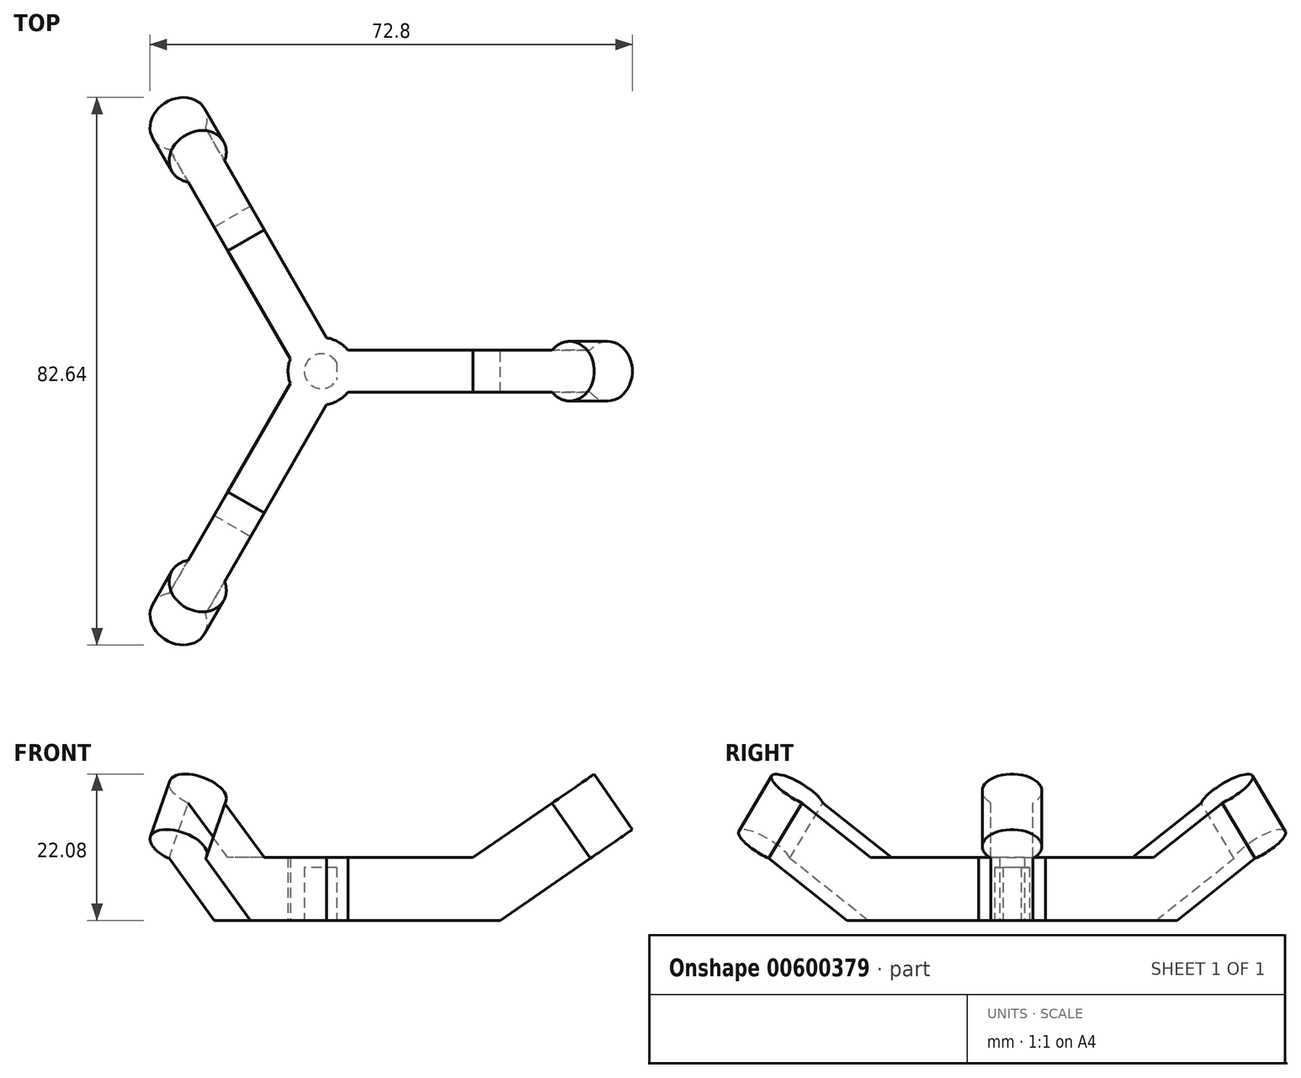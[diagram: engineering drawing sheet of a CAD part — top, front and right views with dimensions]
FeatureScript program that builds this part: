
annotation { "Feature Type Name" : "Feature", "Feature Type Description" : "" }
export const myFeature = defineFeature(function(context is Context, id is Id, definition is map)
    precondition{}
    {
        {
            var Q0;
            Q0=qCreatedBy(makeId("Front.planeOp"),FACE);
            var sketch = newSketch(context, id + "F0", { "sketchPlane" : qUnion([Q0])});
            skCircle(sketch, "E0", {"center": v(0, 59.06) * mm, "radius": 63.5 * mm, "construction": true});
            skCircle(sketch, "E1", {"center": v(38.1, 3.57) * mm, "radius": 5 * mm, "construction": true});
            skLineSegment(sketch, "E2", {"start": v(33.16, 2.82) * mm, "end": v(40.58, 7.9) * mm, "construction": true});
            skLineSegment(sketch, "E3", {"start": v(33.16, 2.82) * mm, "end": v(33.72, 2) * mm, "construction": true});
            skLineSegment(sketch, "E4", {"start": v(33.72, 2) * mm, "end": v(41.14, 7.09) * mm, "construction": true});
            skLineSegment(sketch, "E5", {"start": v(41.14, 7.09) * mm, "end": v(40.58, 7.9) * mm, "construction": true});
            skLineSegment(sketch, "E6", {"start": v(38.1, 3.57) * mm, "end": v(0, 59.06) * mm, "construction": true});
            skLineSegment(sketch, "E7", {"start": v(0, -6.99) * mm, "end": v(2.63, -6.99) * mm});
            skLineSegment(sketch, "E8", {"start": v(2.63, -6.99) * mm, "end": v(2.63, -14.99) * mm});
            skLineSegment(sketch, "E9", {"start": v(0, -6.99) * mm, "end": v(0, -5.49) * mm});
            skLineSegment(sketch, "E10", {"start": v(0, -5.49) * mm, "end": v(22.83, -5.49) * mm});
            skLineSegment(sketch, "E11", {"start": v(22.83, -5.49) * mm, "end": v(33.72, 2) * mm});
            skLineSegment(sketch, "E12", {"start": v(33.72, 2) * mm, "end": v(41.14, 7.09) * mm});
            skLineSegment(sketch, "E13", {"start": v(2.63, -14.99) * mm, "end": v(26.95, -14.98) * mm});
            skLineSegment(sketch, "E14", {"start": v(26.95, -14.98) * mm, "end": v(46.9, -1.3) * mm});
            skLineSegment(sketch, "E15", {"start": v(46.9, -1.3) * mm, "end": v(41.14, 7.09) * mm});
            skLineSegment(sketch, "E16", {"start": v(0, 0) * mm, "end": v(0, -5.49) * mm, "construction": true});
            skSolve(sketch);
        }
        {
            var Q0;
            Q0 = qSketchRegion(id + "F0", true);
            extrude(context, id + "F1", {"entities" : qUnion([Q0]), "endBound" : BoundingType.SYMMETRIC, "depth" : 6.35 * mm, "offsetDistance" : 25.4 * mm});
        }
        {
            var Q0;
            Q0=makeQuery(id+"F1.opExtrude","SWEPT_FACE",FACE,{"disambiguationData":[OSD([sQuery(id+"F0.wireOp",EDGE,"E11"),sQuery(id+"F0.wireOp",EDGE,"E12")])]});
            var sketch = newSketch(context, id + "F2", { "sketchPlane" : qUnion([Q0])});
            skLineSegment(sketch, "E17.0", {"start": v(37.93, -3.18) * mm, "end": v(37.93, 3.17) * mm});
            skLineSegment(sketch, "E18.0", {"start": v(15.72, 3.18) * mm, "end": v(37.93, 3.18) * mm});
            skLineSegment(sketch, "E19.0", {"start": v(15.72, -3.18) * mm, "end": v(37.93, -3.18) * mm});
            skCircle(sketch, "E20", {"center": v(33.43, 0) * mm, "radius": 4.5 * mm});
            skSolve(sketch);
        }
        {
            var Q0;
            {var subQ0=sQuery(id+"F2.wireOp",EDGE,"E20");var subQ1=sQuery(id+"F2.wireOp",EDGE,"E18.0");var subQ2=makeQuery(id+"F2.imprint","INTERSECT",VERTEX,{"disambiguationData":[OD(0.0)],"derivedFrom":[subQ1,subQ0]});Q0=makeQuery(id+"F2.imprint","IMPRINT",FACE,{"disambiguationData":[TD([[makeQuery(id+"F2.imprint","IMPRINT",EDGE,{"disambiguationData":[TD([[subQ2,-1.0]])],"derivedFrom":subQ1}),1.0]])]});}
            var Q1;
            {var subQ0=sQuery(id+"F2.wireOp",EDGE,"E20");var subQ1=sQuery(id+"F2.wireOp",EDGE,"E19.0");var subQ2=makeQuery(id+"F2.imprint","INTERSECT",VERTEX,{"disambiguationData":[OD(0.0)],"derivedFrom":[subQ1,subQ0]});Q1=makeQuery(id+"F2.imprint","IMPRINT",FACE,{"disambiguationData":[TD([[makeQuery(id+"F2.imprint","IMPRINT",EDGE,{"disambiguationData":[TD([[subQ2,-1.0]])],"derivedFrom":subQ1}),-1.0]])]});}
            var Q2;
            {var subQ0=sQuery(id+"F2.wireOp",EDGE,"E20");var subQ1=sQuery(id+"F2.wireOp",EDGE,"E18.0");var subQ2=makeQuery(id+"F2.imprint","INTERSECT",VERTEX,{"disambiguationData":[OD(0.0)],"derivedFrom":[subQ1,subQ0]});Q2=makeQuery(id+"F2.imprint","IMPRINT",FACE,{"disambiguationData":[TD([[makeQuery(id+"F2.imprint","IMPRINT",EDGE,{"disambiguationData":[TD([[subQ2,-1.0]])],"derivedFrom":subQ1}),-1.0]])]});}
            var Q3;
            Q3=makeQuery(id+"F1.opExtrude","SWEPT_FACE",FACE,{"disambiguationData":[OSD([sQuery(id+"F0.wireOp",EDGE,"E14")])]});
            extrude(context, id + "F3", {"entities" : qUnion([Q0, Q1, Q2]), "operationType" : NewBodyOperationType.ADD, "endBound" : BoundingType.UP_TO_SURFACE, "oppositeDirection" : true, "depth" : 25.4 * mm, "endBoundEntityFace" : qUnion([Q3]), "offsetDistance" : 25.4 * mm});
        }
        {
            var Q0;
            Q0=makeQuery(id+"F3.boolean.opBoolean","MERGE",FACE,{"derivedFrom":[makeQuery(id+"F1.opExtrude","SWEPT_FACE",FACE,{"disambiguationData":[OSD([sQuery(id+"F0.wireOp",EDGE,"E11"),sQuery(id+"F0.wireOp",EDGE,"E12")])]}),makeQuery(id+"F3.opExtrude","CAP_FACE",FACE,{"disambiguationData":[OSD([sQuery(id+"F2.wireOp",EDGE,"E20")])],"isStart":true})]});
            var sketch = newSketch(context, id + "F4", { "sketchPlane" : qUnion([Q0])});
            skLineSegment(sketch, "E21.0.0", {"start": v(37.93, -3.18) * mm, "end": v(37.93, 3.17) * mm});
            skLineSegment(sketch, "E21.0.1", {"start": v(37.93, 3.18) * mm, "end": v(36.62, 3.18) * mm});
            skArc(sketch, "E21.0.2", {"start": v(36.62, 3.17) * mm, "mid": v(33.43, 4.5) * mm, "end": v(30.24, 3.18) * mm});
            skLineSegment(sketch, "E21.0.3", {"start": v(30.24, 3.18) * mm, "end": v(15.72, 3.18) * mm});
            skLineSegment(sketch, "E21.0.4", {"start": v(15.72, 3.17) * mm, "end": v(15.72, -3.18) * mm});
            skLineSegment(sketch, "E21.0.5", {"start": v(15.72, -3.18) * mm, "end": v(30.24, -3.18) * mm});
            skArc(sketch, "E21.0.6", {"start": v(30.24, -3.18) * mm, "mid": v(33.43, -4.5) * mm, "end": v(36.62, -3.17) * mm});
            skLineSegment(sketch, "E21.0.7", {"start": v(36.62, -3.18) * mm, "end": v(37.93, -3.18) * mm});
            skCircle(sketch, "E22", {"center": v(33.43, 0) * mm, "radius": 4.5 * mm});
            skSolve(sketch);
        }
        {
            var Q0;
            {var subQ0=sQuery(id+"F4.wireOp",EDGE,"E21.0.7");Q0=makeQuery(id+"F4.imprint","IMPRINT",FACE,{"disambiguationData":[TD([[makeQuery(id+"F4.imprint","IMPRINT",EDGE,{"derivedFrom":subQ0}),1.0]])]});}
            var Q1;
            {var subQ0=sQuery(id+"F4.wireOp",EDGE,"E21.0.1");Q1=makeQuery(id+"F4.imprint","IMPRINT",FACE,{"disambiguationData":[TD([[makeQuery(id+"F4.imprint","IMPRINT",EDGE,{"derivedFrom":subQ0}),-1.0]])]});}
            extrude(context, id + "F5", {"entities" : qUnion([Q0, Q1]), "operationType" : NewBodyOperationType.REMOVE, "endBound" : BoundingType.THROUGH_ALL, "oppositeDirection" : true, "depth" : 25.4 * mm, "offsetDistance" : 25.4 * mm});
        }
        {
            var Q0;
            Q0=makeQuery(id+"F1.opExtrude","SWEPT_BODY",BODY,{"disambiguationData":[OSD([sQuery(id+"F0.wireOp",EDGE,"E7"),sQuery(id+"F0.wireOp",EDGE,"E8"),sQuery(id+"F0.wireOp",EDGE,"E9"),sQuery(id+"F0.wireOp",EDGE,"E10"),sQuery(id+"F0.wireOp",EDGE,"E11"),sQuery(id+"F0.wireOp",EDGE,"E12"),sQuery(id+"F0.wireOp",EDGE,"E13"),sQuery(id+"F0.wireOp",EDGE,"E14"),sQuery(id+"F0.wireOp",EDGE,"E15")])]});
            var Q1;
            Q1=sQuery(id+"F0.wireOp",EDGE,"E16");
            circularPattern(context, id + "F6", {"operationType" : NewBodyOperationType.ADD, "entities" : qUnion([Q0]), "axis" : qUnion([Q1]), "angle" : 360 * degree, "instanceCount" : 3, "equalSpace" : true});
        }
        {
            var Q0;
            Q0=makeQuery(id+"F1.opExtrude","SWEPT_FACE",FACE,{"disambiguationData":[OSD([sQuery(id+"F0.wireOp",EDGE,"E13")])]});
            var sketch = newSketch(context, id + "F7", { "sketchPlane" : qUnion([Q0])});
            skCircle(sketch, "E23", {"center": v(0, 0) * mm, "radius": 2.62 * mm});
            skLineSegment(sketch, "E24.0.0", {"start": v(1.44, 3.86) * mm, "end": v(-10.72, 24.93) * mm});
            skLineSegment(sketch, "E24.0.1", {"start": v(-10.72, 24.93) * mm, "end": v(-16.22, 21.75) * mm});
            skLineSegment(sketch, "E24.0.2", {"start": v(-16.22, 21.75) * mm, "end": v(-4.06, 0.69) * mm});
            skLineSegment(sketch, "E24.0.3", {"start": v(-4.06, 0.69) * mm, "end": v(1.44, 3.86) * mm});
            skCircle(sketch, "E25", {"center": v(0, 0) * mm, "radius": 5.08 * mm});
            skSolve(sketch);
        }
        {
            var Q0;
            {var subQ0=sQuery(id+"F7.wireOp",EDGE,"E24.0.3");var subQ1=sQuery(id+"F7.wireOp",EDGE,"E23");var subQ2=makeQuery(id+"F7.imprint","INTERSECT",VERTEX,{"derivedFrom":[subQ1,subQ0]});Q0=makeQuery(id+"F7.imprint","IMPRINT",FACE,{"disambiguationData":[TD([[makeQuery(id+"F7.imprint","IMPRINT",EDGE,{"disambiguationData":[TD([[subQ2,1.0]])],"derivedFrom":subQ1}),-1.0]])]});}
            var Q1;
            {var subQ0=sQuery(id+"F7.wireOp",EDGE,"E24.0.3");var subQ1=sQuery(id+"F7.wireOp",EDGE,"E23");var subQ2=makeQuery(id+"F7.imprint","INTERSECT",VERTEX,{"derivedFrom":[subQ1,subQ0]});Q1=makeQuery(id+"F7.imprint","IMPRINT",FACE,{"disambiguationData":[TD([[makeQuery(id+"F7.imprint","IMPRINT",EDGE,{"disambiguationData":[TD([[subQ2,-1.0]])],"derivedFrom":subQ1}),-1.0]])]});}
            var Q2;
            {var subQ0=makeQuery(id+"F1.opExtrude","SWEPT_FACE",FACE,{"disambiguationData":[OSD([sQuery(id+"F0.wireOp",EDGE,"E10")])]});Q2=makeQuery(id+"F6.boolean.opBoolean","MERGE",FACE,{"derivedFrom":[subQ0,makeQuery(id+"F6.opPattern","COPY",FACE,{"derivedFrom":subQ0,"instanceName":"1"}),makeQuery(id+"F6.opPattern","COPY",FACE,{"derivedFrom":subQ0,"instanceName":"2"})]});}
            extrude(context, id + "F8", {"entities" : qUnion([Q0, Q1]), "operationType" : NewBodyOperationType.ADD, "endBound" : BoundingType.UP_TO_SURFACE, "oppositeDirection" : true, "depth" : 25.4 * mm, "endBoundEntityFace" : qUnion([Q2]), "offsetDistance" : 25.4 * mm});
        }
        {
            var Q0;
            {var subQ0=sQuery(id+"F7.wireOp",EDGE,"E25");var subQ1=sQuery(id+"F0.wireOp",EDGE,"E13");var subQ2=sQuery(id+"F0.wireOp",EDGE,"E8");var subQ3=makeQuery(id+"F1.opExtrude","SWEPT_EDGE",EDGE,{"disambiguationData":[OSD([subQ2,subQ1])]});var subQ5=sQuery(id+"F7.wireOp",EDGE,"E23");var subQ6=makeQuery(id+"F7.imprint","INTERSECT",VERTEX,{"derivedFrom":[subQ3,subQ5]});var subQ7=sQuery(id+"F7.wireOp",EDGE,"E24.0.3");var subQ8=makeQuery(id+"F7.imprint","INTERSECT",VERTEX,{"derivedFrom":[sQuery(id+"F7.wireOp",EDGE,"E24.0.2"),subQ7,subQ0]});var subQ9=makeQuery(id+"F7.imprint","INTERSECT",VERTEX,{"derivedFrom":[subQ5,subQ7]});var subQ11=makeQuery(id+"F7.imprint","INTERSECT",VERTEX,{"derivedFrom":[sQuery(id+"F7.wireOp",EDGE,"E24.0.0"),subQ7,subQ0]});var subQ12=makeQuery(id+"F1.opExtrude","SWEPT_FACE",FACE,{"disambiguationData":[OSD([subQ1])]});Q0=makeQuery(id+"F8.boolean.opBoolean","MERGE",FACE,{"derivedFrom":[subQ12,makeQuery(id+"F6.opPattern","COPY",FACE,{"derivedFrom":subQ12,"instanceName":"1"}),makeQuery(id+"F6.opPattern","COPY",FACE,{"derivedFrom":subQ12,"instanceName":"2"}),makeQuery(id+"F8.opExtrude","CAP_FACE",FACE,{"disambiguationData":[OSD([subQ2,subQ1,subQ5,subQ7,subQ0]),TDD([makeQuery(id+"F7.imprint","IMPRINT",EDGE,{"disambiguationData":[TD([[subQ9,1.0]])],"derivedFrom":subQ5}),makeQuery(id+"F7.imprint","IMPRINT",EDGE,{"disambiguationData":[TD([[subQ9,-1.0]])],"derivedFrom":subQ7}),makeQuery(id+"F7.imprint","IMPRINT",EDGE,{"disambiguationData":[TD([[subQ11,1.0]])],"derivedFrom":subQ0}),makeQuery(id+"F7.imprint","IMPRINT",EDGE,{"disambiguationData":[TD([[subQ6,1.0]])],"derivedFrom":subQ3})])],"isStart":true}),makeQuery(id+"F8.opExtrude","CAP_FACE",FACE,{"disambiguationData":[OSD([subQ2,subQ1,subQ5,subQ7,subQ0]),TDD([makeQuery(id+"F7.imprint","IMPRINT",EDGE,{"disambiguationData":[TD([[subQ9,-1.0]])],"derivedFrom":subQ5}),makeQuery(id+"F7.imprint","IMPRINT",EDGE,{"disambiguationData":[TD([[subQ9,1.0]])],"derivedFrom":subQ7}),makeQuery(id+"F7.imprint","IMPRINT",EDGE,{"disambiguationData":[TD([[subQ8,-1.0]])],"derivedFrom":subQ0}),makeQuery(id+"F7.imprint","IMPRINT",EDGE,{"disambiguationData":[TD([[subQ6,-1.0]])],"derivedFrom":subQ3})])],"isStart":true})]});}
            var sketch = newSketch(context, id + "F9", { "sketchPlane" : qUnion([Q0])});
            skCircle(sketch, "E26.0", {"center": v(0, 0) * mm, "radius": 2.62 * mm});
            skLineSegment(sketch, "E27", {"start": v(2.25, 1.35) * mm, "end": v(2.25, -1.35) * mm});
            skSolve(sketch);
        }
        {
            var Q0;
            {var subQ0=sQuery(id+"F9.wireOp",EDGE,"E27");Q0=makeQuery(id+"F9.imprint","IMPRINT",FACE,{"disambiguationData":[TD([[makeQuery(id+"F9.imprint","IMPRINT",EDGE,{"derivedFrom":subQ0}),1.0]])]});}
            var Q1;
            {var subQ0=sQuery(id+"F0.wireOp",EDGE,"E10");var subQ1=makeQuery(id+"F1.opExtrude","SWEPT_FACE",FACE,{"disambiguationData":[OSD([subQ0])]});Q1=makeQuery(id+"F8.boolean.opBoolean","MERGE",FACE,{"derivedFrom":[makeQuery(id+"F6.boolean.opBoolean","MERGE",FACE,{"derivedFrom":[subQ1,makeQuery(id+"F6.opPattern","COPY",FACE,{"derivedFrom":subQ1,"instanceName":"1"}),makeQuery(id+"F6.opPattern","COPY",FACE,{"derivedFrom":subQ1,"instanceName":"2"})]}),makeQuery(id+"F8.opExtrude","CAP_FACE",FACE,{"disambiguationData":[OSD([subQ0]),OD(0.0)],"isStart":false}),makeQuery(id+"F8.opExtrude","CAP_FACE",FACE,{"disambiguationData":[OSD([subQ0]),OD(1.0)],"isStart":false})]});}
            extrude(context, id + "F10", {"entities" : qUnion([Q0]), "operationType" : NewBodyOperationType.ADD, "endBound" : BoundingType.UP_TO_SURFACE, "oppositeDirection" : true, "depth" : 25.4 * mm, "endBoundEntityFace" : qUnion([Q1]), "offsetDistance" : 25.4 * mm});
        }
    });
